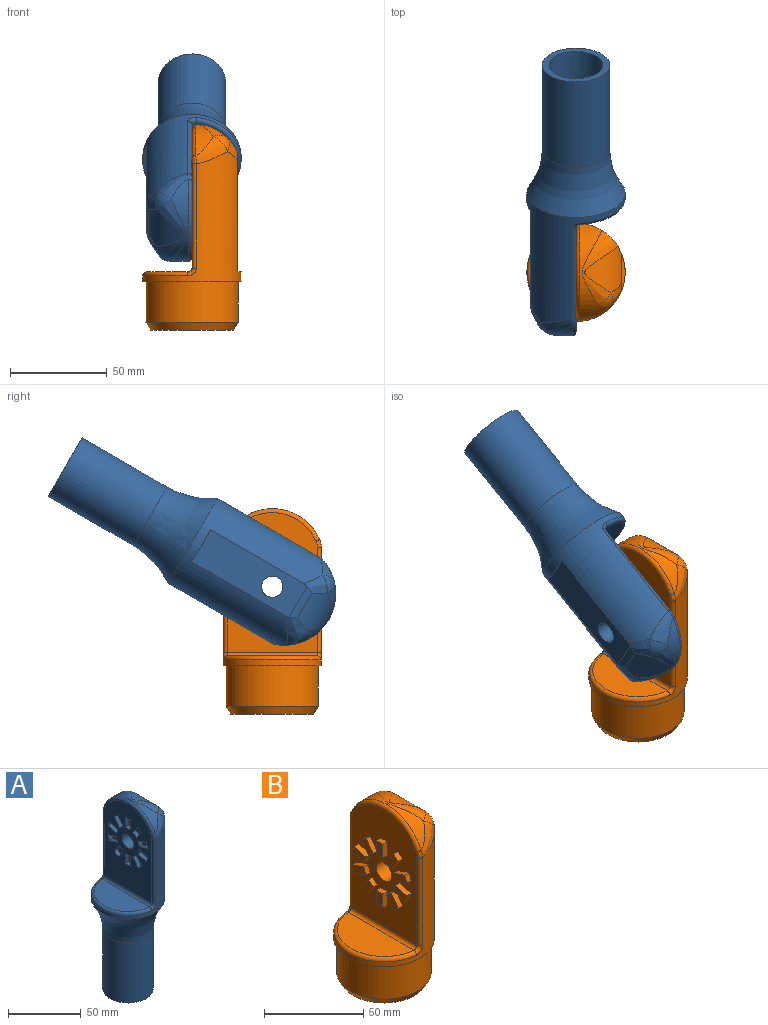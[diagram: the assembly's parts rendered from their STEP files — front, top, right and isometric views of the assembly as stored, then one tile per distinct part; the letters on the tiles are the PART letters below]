
ASSEMBLY  parts=2 mates=1
PART A: 77 faces, bbox 66.3x66.3x159.7 mm
  f0: plane 72.06x46.63mm, normal (-1,0,0), area 2677.3mm2, adj f10,f18,f19,f20,f21,f23,f24,f25
  f1: cylinder r=25.4mm len=69.29mm, axis (0,0,-1), area 3964mm2, adj f2,f3,f8,f12,f13,f17,f68,f69
  f2: plane 57.87x19.49mm, normal (1,0,0), area 1015.9mm2, adj f1,f8,f10,f12,f15,f17
  f3: cylinder r=26.67mm len=49.74mm, axis (-1,0,0), area 337.2mm2, adj f1,f12,f13,f14,f75,f76
  f4: plane 46.63x21.4mm, normal (0,0,1), area 766.6mm2, adj f70,f71
  f5: cylinder r=13.97mm len=76.2mm, axis (0,0,1), area 6688.5mm2, adj f7,f9
  f6: cylinder r=17.47mm len=50.69mm, axis (0,0,1), area 5564mm2, adj f7,f68
  f7: plane 34.94x34.94mm, normal (0,0,-1), area 345.7mm2, adj f5,f6
  f8: plane 19.28x1.9mm, normal (0,0,1), area 24.6mm2, adj f1,f2
  f9: plane 27.94x27.94mm, normal (0,0,-1), area 613.1mm2, adj f5
  f10: cylinder r=5.5mm len=23.5mm, axis (-1,0,0), area 812.1mm2, adj f0,f2
  f11: cylinder r=24.43mm len=22.18mm, axis (0,-1,0), area 364.7mm2, adj f12,f14,f15,f17
  f12: bspline ~18.71x17.31mm, area 126.9mm2, adj f1,f2,f3,f11,f14,f15
  f13: bspline ~18.71x14.78mm, area 119.3mm2, adj f1,f3,f16,f74
  f14: bspline ~41.98x20.04mm, area 268.2mm2, adj f3,f11,f12,f16
  f15: cylinder r=10mm len=18.52mm, axis (0,-1,0), area 69.4mm2, adj f2,f11,f12,f17
  f16: sphere r=10mm, area 48.8mm2, adj f13,f14,f17
  f17: bspline ~15.1x13.94mm, area 86.2mm2, adj f1,f2,f11,f15,f16
  f18: plane 8x3mm, normal (0,0.31,-0.95), area 25.2mm2, adj f0,f19,f21,f22
  f19: plane 4.28x3mm, normal (0,-0.95,-0.31), area 13.5mm2, adj f0,f18,f20,f22
  f20: plane 8x3mm, normal (0,-0.31,0.95), area 25.2mm2, adj f0,f19,f21,f22
  f21: plane 4.28x3mm, normal (0,0.95,0.31), area 13.5mm2, adj f0,f18,f20,f22
  f22: plane 9.39x6.88mm, normal (-1,0,0), area 37.9mm2, adj f18,f19,f20,f21
  f23: plane 8x3mm, normal (0,-0.31,-0.95), area 25.2mm2, adj f0,f24,f26,f27
  f24: plane 4.28x3mm, normal (0,-0.95,0.31), area 13.5mm2, adj f0,f23,f25,f27
  f25: plane 8x3mm, normal (0,0.31,0.95), area 25.2mm2, adj f0,f24,f26,f27
  f26: plane 4.28x3mm, normal (0,0.95,-0.31), area 13.5mm2, adj f0,f23,f25,f27
  f27: plane 9.39x6.88mm, normal (-1,0,0), area 37.9mm2, adj f23,f24,f25,f26
  f28: plane 6.81x4.95mm, normal (0,-0.81,-0.59), area 25.2mm2, adj f0,f29,f31,f32
  f29: plane 3.64x3mm, normal (0,-0.59,0.81), area 13.5mm2, adj f0,f28,f30,f32
  f30: plane 6.81x4.95mm, normal (0,0.81,0.59), area 25.2mm2, adj f0,f29,f31,f32
  f31: plane 3.64x3mm, normal (0,0.59,-0.81), area 13.5mm2, adj f0,f28,f30,f32
  f32: plane 9.45x8.59mm, normal (-1,0,0), area 37.9mm2, adj f28,f29,f30,f31
  f33: plane 8.41x3mm, normal (0,-1,0), area 25.2mm2, adj f0,f34,f36,f37
  f34: plane 4.5x3mm, normal (0,0,1), area 13.5mm2, adj f0,f33,f35,f37
  f35: plane 8.41x3mm, normal (0,1,0), area 25.2mm2, adj f0,f34,f36,f37
  f36: plane 4.5x3mm, normal (0,0,-1), area 13.5mm2, adj f0,f33,f35,f37
  f37: plane 8.41x4.5mm, normal (-1,0,0), area 37.9mm2, adj f33,f34,f35,f36
  f38: plane 8x3mm, normal (0,-0.31,0.95), area 25.2mm2, adj f0,f39,f41,f42
  f39: plane 4.28x3mm, normal (0,0.95,0.31), area 13.5mm2, adj f0,f38,f40,f42
  f40: plane 8x3mm, normal (0,0.31,-0.95), area 25.2mm2, adj f0,f39,f41,f42
  f41: plane 4.28x3mm, normal (0,-0.95,-0.31), area 13.5mm2, adj f0,f38,f40,f42
  f42: plane 9.39x6.88mm, normal (-1,0,0), area 37.9mm2, adj f38,f39,f40,f41
  f43: plane 6.81x4.95mm, normal (0,-0.81,0.59), area 25.2mm2, adj f0,f44,f46,f47
  f44: plane 3.64x3mm, normal (0,0.59,0.81), area 13.5mm2, adj f0,f43,f45,f47
  f45: plane 6.81x4.95mm, normal (0,0.81,-0.59), area 25.2mm2, adj f0,f44,f46,f47
  f46: plane 3.64x3mm, normal (0,-0.59,-0.81), area 13.5mm2, adj f0,f43,f45,f47
  f47: plane 9.45x8.59mm, normal (-1,0,0), area 37.9mm2, adj f43,f44,f45,f46
  f48: plane 6.81x4.95mm, normal (0,0.81,0.59), area 25.2mm2, adj f0,f49,f51,f52
  f49: plane 3.64x3mm, normal (0,0.59,-0.81), area 13.5mm2, adj f0,f48,f50,f52
  f50: plane 6.81x4.95mm, normal (0,-0.81,-0.59), area 25.2mm2, adj f0,f49,f51,f52
  f51: plane 3.64x3mm, normal (0,-0.59,0.81), area 13.5mm2, adj f0,f48,f50,f52
  f52: plane 9.45x8.59mm, normal (-1,0,0), area 37.9mm2, adj f48,f49,f50,f51
  f53: plane 8x3mm, normal (0,0.31,0.95), area 25.2mm2, adj f0,f54,f56,f57
  f54: plane 4.28x3mm, normal (0,0.95,-0.31), area 13.5mm2, adj f0,f53,f55,f57
  f55: plane 8x3mm, normal (0,-0.31,-0.95), area 25.2mm2, adj f0,f54,f56,f57
  f56: plane 4.28x3mm, normal (0,-0.95,0.31), area 13.5mm2, adj f0,f53,f55,f57
  f57: plane 9.39x6.88mm, normal (-1,0,0), area 37.9mm2, adj f53,f54,f55,f56
  f58: plane 4.5x3mm, normal (0,0,1), area 13.5mm2, adj f0,f59,f61,f62
  f59: plane 8.41x3mm, normal (0,1,0), area 25.2mm2, adj f0,f58,f60,f62
  f60: plane 4.5x3mm, normal (0,0,-1), area 13.5mm2, adj f0,f59,f61,f62
  f61: plane 8.41x3mm, normal (0,-1,0), area 25.2mm2, adj f0,f58,f60,f62
  f62: plane 8.41x4.5mm, normal (-1,0,0), area 37.9mm2, adj f58,f59,f60,f61
  f63: plane 6.81x4.95mm, normal (0,0.81,-0.59), area 25.2mm2, adj f0,f64,f66,f67
  f64: plane 3.64x3mm, normal (0,-0.59,-0.81), area 13.5mm2, adj f0,f63,f65,f67
  f65: plane 6.81x4.95mm, normal (0,-0.81,0.59), area 25.2mm2, adj f0,f64,f66,f67
  f66: plane 3.64x3mm, normal (0,0.59,0.81), area 13.5mm2, adj f0,f63,f65,f67
  f67: plane 9.45x8.59mm, normal (-1,0,0), area 37.9mm2, adj f63,f64,f65,f66
  f68: torus R=62.47mm, axis (0,0,1), area 3433.3mm2, adj f1,f6
  f69: bspline ~5.06x4.9mm, area 14.2mm2, adj f1,f70,f71,f72
  f70: cylinder r=2mm len=46.63mm, axis (0,-1,0), area 146.5mm2, adj f0,f4,f69,f73
  f71: torus R=23.4mm, axis (0,0,1), area 230.2mm2, adj f1,f4,f69,f73
  f72: cylinder r=2mm len=53.91mm, axis (0,0,-1), area 178.6mm2, adj f0,f1,f69,f74
  f73: bspline ~5.31x4.64mm, area 14.2mm2, adj f1,f70,f71,f75
  f74: bspline ~8.63x3.92mm, area 13mm2, adj f0,f13,f72,f76
  f75: cylinder r=2mm len=55.81mm, axis (0,0,-1), area 184.3mm2, adj f0,f1,f3,f73,f76
  f76: torus R=24.67mm, axis (-1,0,0), area 195.8mm2, adj f0,f3,f74,f75
PART B: 77 faces, bbox 55.4x57.3x110.8 mm
  f0: plane 72.06x46.63mm, normal (-1,0,0), area 2677.3mm2, adj f12,f18,f19,f20,f21,f23,f24,f25
  f1: cylinder r=25.4mm len=72.07mm, axis (0,0,-1), area 4078.6mm2, adj f2,f3,f5,f9,f13,f14,f15,f17
  f2: plane 64.24x21.77mm, normal (1,0,0), area 1092.4mm2, adj f1,f5,f12,f13,f17
  f3: cylinder r=26.67mm len=49.74mm, axis (-1,0,0), area 370.8mm2, adj f1,f14,f15,f74,f75
  f4: plane 46.63x21.4mm, normal (0,0,1), area 766.6mm2, adj f69,f70
  f5: plane 19.28x1.9mm, normal (0,0,1), area 24.6mm2, adj f1,f2
  f6: cylinder r=21.5mm len=43mm, axis (0,0,1), area 675.4mm2, adj f8,f76
  f7: cylinder r=23.81mm len=47.63mm, axis (0,0,1), area 3142mm2, adj f9,f11
  f8: plane 43.01x43.01mm, normal (0,0,-1), area 0.4mm2, adj f6,f11
  f9: plane 50.8x50.8mm, normal (0,0,-1), area 245.4mm2, adj f1,f7
  f10: plane 3x3mm, normal (0,0,-1), area 7.1mm2, adj f76
  f11: cone r=23.81mm half-angle=30deg, axis (0,0,1), area 657.5mm2, adj f7,f8
  f12: cylinder r=5.5mm len=23.5mm, axis (-1,0,0), area 812.1mm2, adj f0,f2
  f13: cylinder r=24.43mm len=23.81mm, axis (0,-1,0), area 378.5mm2, adj f1,f2,f15,f17
  f14: bspline ~19.45x15.42mm, area 131.4mm2, adj f1,f3,f16,f73
  f15: bspline ~40.62x19.29mm, area 283.5mm2, adj f1,f3,f13,f16
  f16: sphere r=10mm, area 50.1mm2, adj f14,f15,f17
  f17: bspline ~13.55x13.2mm, area 85.5mm2, adj f1,f2,f13,f16
  f18: plane 4.5x3mm, normal (0,0,-1), area 13.5mm2, adj f0,f19,f21,f22
  f19: plane 8.41x3mm, normal (0,-1,0), area 25.2mm2, adj f0,f18,f20,f22
  f20: plane 4.5x3mm, normal (0,0,1), area 13.5mm2, adj f0,f19,f21,f22
  f21: plane 8.41x3mm, normal (0,1,0), area 25.2mm2, adj f0,f18,f20,f22
  f22: plane 8.41x4.5mm, normal (-1,0,0), area 37.9mm2, adj f18,f19,f20,f21
  f23: plane 6.81x4.95mm, normal (0,-0.81,0.59), area 25.2mm2, adj f0,f24,f26,f27
  f24: plane 3.64x3mm, normal (0,0.59,0.81), area 13.5mm2, adj f0,f23,f25,f27
  f25: plane 6.81x4.95mm, normal (0,0.81,-0.59), area 25.2mm2, adj f0,f24,f26,f27
  f26: plane 3.64x3mm, normal (0,-0.59,-0.81), area 13.5mm2, adj f0,f23,f25,f27
  f27: plane 9.45x8.59mm, normal (-1,0,0), area 37.9mm2, adj f23,f24,f25,f26
  f28: plane 8x3mm, normal (0,-0.31,0.95), area 25.2mm2, adj f0,f29,f31,f32
  f29: plane 4.28x3mm, normal (0,0.95,0.31), area 13.5mm2, adj f0,f28,f30,f32
  f30: plane 8x3mm, normal (0,0.31,-0.95), area 25.2mm2, adj f0,f29,f31,f32
  f31: plane 4.28x3mm, normal (0,-0.95,-0.31), area 13.5mm2, adj f0,f28,f30,f32
  f32: plane 9.39x6.88mm, normal (-1,0,0), area 37.9mm2, adj f28,f29,f30,f31
  f33: plane 8x3mm, normal (0,0.31,0.95), area 25.2mm2, adj f0,f34,f36,f37
  f34: plane 4.28x3mm, normal (0,0.95,-0.31), area 13.5mm2, adj f0,f33,f35,f37
  f35: plane 8x3mm, normal (0,-0.31,-0.95), area 25.2mm2, adj f0,f34,f36,f37
  f36: plane 4.28x3mm, normal (0,-0.95,0.31), area 13.5mm2, adj f0,f33,f35,f37
  f37: plane 9.39x6.88mm, normal (-1,0,0), area 37.9mm2, adj f33,f34,f35,f36
  f38: plane 6.81x4.95mm, normal (0,0.81,0.59), area 25.2mm2, adj f0,f39,f41,f42
  f39: plane 3.64x3mm, normal (0,0.59,-0.81), area 13.5mm2, adj f0,f38,f40,f42
  f40: plane 6.81x4.95mm, normal (0,-0.81,-0.59), area 25.2mm2, adj f0,f39,f41,f42
  f41: plane 3.64x3mm, normal (0,-0.59,0.81), area 13.5mm2, adj f0,f38,f40,f42
  f42: plane 9.45x8.59mm, normal (-1,0,0), area 37.9mm2, adj f38,f39,f40,f41
  f43: plane 8.41x3mm, normal (0,1,0), area 25.2mm2, adj f0,f44,f46,f47
  f44: plane 4.5x3mm, normal (0,0,-1), area 13.5mm2, adj f0,f43,f45,f47
  f45: plane 8.41x3mm, normal (0,-1,0), area 25.2mm2, adj f0,f44,f46,f47
  f46: plane 4.5x3mm, normal (0,0,1), area 13.5mm2, adj f0,f43,f45,f47
  f47: plane 8.41x4.5mm, normal (-1,0,0), area 37.9mm2, adj f43,f44,f45,f46
  f48: plane 6.81x4.95mm, normal (0,0.81,-0.59), area 25.2mm2, adj f0,f49,f51,f52
  f49: plane 3.64x3mm, normal (0,-0.59,-0.81), area 13.5mm2, adj f0,f48,f50,f52
  f50: plane 6.81x4.95mm, normal (0,-0.81,0.59), area 25.2mm2, adj f0,f49,f51,f52
  f51: plane 3.64x3mm, normal (0,0.59,0.81), area 13.5mm2, adj f0,f48,f50,f52
  f52: plane 9.45x8.59mm, normal (-1,0,0), area 37.9mm2, adj f48,f49,f50,f51
  f53: plane 8x3mm, normal (0,0.31,-0.95), area 25.2mm2, adj f0,f54,f56,f57
  f54: plane 4.28x3mm, normal (0,-0.95,-0.31), area 13.5mm2, adj f0,f53,f55,f57
  f55: plane 8x3mm, normal (0,-0.31,0.95), area 25.2mm2, adj f0,f54,f56,f57
  f56: plane 4.28x3mm, normal (0,0.95,0.31), area 13.5mm2, adj f0,f53,f55,f57
  f57: plane 9.39x6.88mm, normal (-1,0,0), area 37.9mm2, adj f53,f54,f55,f56
  f58: plane 8x3mm, normal (0,-0.31,-0.95), area 25.2mm2, adj f0,f59,f61,f62
  f59: plane 4.28x3mm, normal (0,-0.95,0.31), area 13.5mm2, adj f0,f58,f60,f62
  f60: plane 8x3mm, normal (0,0.31,0.95), area 25.2mm2, adj f0,f59,f61,f62
  f61: plane 4.28x3mm, normal (0,0.95,-0.31), area 13.5mm2, adj f0,f58,f60,f62
  f62: plane 9.39x6.88mm, normal (-1,0,0), area 37.9mm2, adj f58,f59,f60,f61
  f63: plane 6.81x4.95mm, normal (0,-0.81,-0.59), area 25.2mm2, adj f0,f64,f66,f67
  f64: plane 3.64x3mm, normal (0,-0.59,0.81), area 13.5mm2, adj f0,f63,f65,f67
  f65: plane 6.81x4.95mm, normal (0,0.81,0.59), area 25.2mm2, adj f0,f64,f66,f67
  f66: plane 3.64x3mm, normal (0,0.59,-0.81), area 13.5mm2, adj f0,f63,f65,f67
  f67: plane 9.45x8.59mm, normal (-1,0,0), area 37.9mm2, adj f63,f64,f65,f66
  f68: bspline ~5.06x4.9mm, area 14.2mm2, adj f1,f69,f70,f71
  f69: cylinder r=2mm len=46.63mm, axis (0,-1,0), area 146.5mm2, adj f0,f4,f68,f72
  f70: torus R=23.4mm, axis (0,0,1), area 230.2mm2, adj f1,f4,f68,f72
  f71: cylinder r=2mm len=53.91mm, axis (0,0,-1), area 178.6mm2, adj f0,f1,f68,f73
  f72: bspline ~5.31x4.64mm, area 14.2mm2, adj f1,f69,f70,f74
  f73: bspline ~8.63x3.92mm, area 13mm2, adj f0,f14,f71,f75
  f74: cylinder r=2mm len=55.81mm, axis (0,0,-1), area 184.3mm2, adj f0,f1,f3,f72,f75
  f75: torus R=24.67mm, axis (-1,0,0), area 195.8mm2, adj f0,f3,f73,f74
  f76: torus R=1.5mm, axis (0,0,1), area 2809.4mm2, adj f6,f10
PLACE A rot(axis=(0,-0.87,0.5),180deg) t=(-1.73,-4.47,98.66)mm
PLACE B t=(-1.73,-45.46,34.26)mm
MATE revolute A.f10 <-> B.f12  axis (1,0,0) through (-1.73,-45.46,74.99)mm
